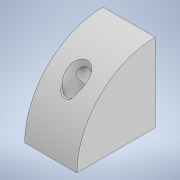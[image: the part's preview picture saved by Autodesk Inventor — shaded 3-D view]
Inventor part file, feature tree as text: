
AUTODESK INVENTOR PART (.ipt)
format: ipt  version: 2021 (Build 250183000, 183)  size: 126,976 bytes
history: native  units: mm
features: sketch x3, plane x2, hole x2, other x1, extrude x1
ambient origin geometry x8: Origin, YZ Plane, XZ Plane, XY Plane, X Axis, Y Axis, Z Axis, Center Point
bodies: Body1 (feature_tree)
feature tree (9):
  other  "實體1"
  extrude  "擠出1"  Depth=30.0mm
  plane  "工作平面1"
  hole  "孔1"  [1 undecoded]
  plane  "工作平面2"
  hole  "孔2"  [1 undecoded]
  sketch  "草圖1"
  sketch  "草圖2"
  sketch  "草圖3"
note: 2 required parameter values undecoded (feature->parameter linkage not recoverable at this tier; creation-order binding heuristic only, values carry confidence <= 0.55)
